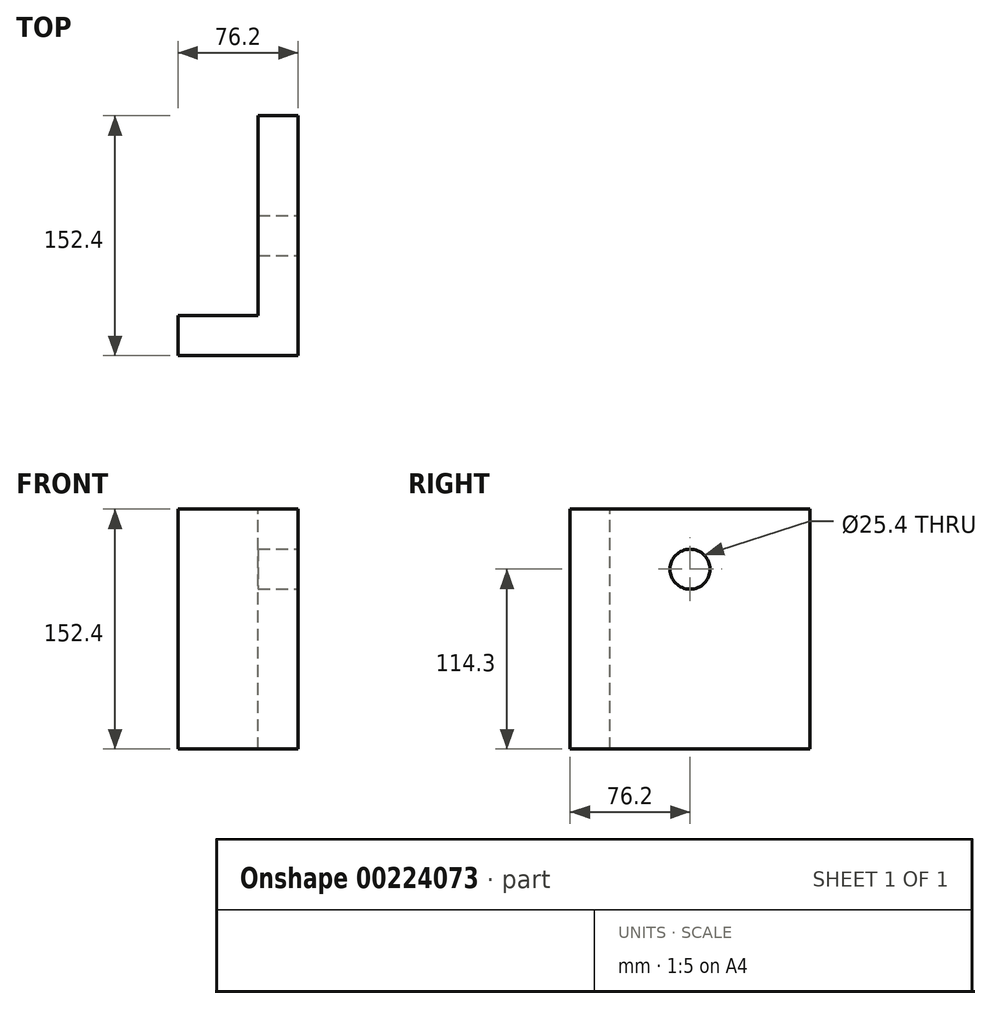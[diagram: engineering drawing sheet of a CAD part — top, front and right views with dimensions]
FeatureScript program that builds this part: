
annotation { "Feature Type Name" : "Feature", "Feature Type Description" : "" }
export const myFeature = defineFeature(function(context is Context, id is Id, definition is map)
    precondition{}
    {
        {
            var Q0;
            Q0=qCreatedBy(makeId("Top.planeOp"),FACE);
            var sketch = newSketch(context, id + "F0", { "sketchPlane" : qUnion([Q0])});
            skLineSegment(sketch, "E0", {"start": v(0, 0) * mm, "end": v(0, 152.4) * mm});
            skLineSegment(sketch, "E1", {"start": v(0, 152.4) * mm, "end": v(-25.4, 152.4) * mm});
            skLineSegment(sketch, "E2", {"start": v(-25.4, 152.4) * mm, "end": v(-25.4, 25.4) * mm});
            skLineSegment(sketch, "E3", {"start": v(-25.4, 25.4) * mm, "end": v(-76.2, 25.4) * mm});
            skLineSegment(sketch, "E4", {"start": v(-76.2, 25.4) * mm, "end": v(-76.2, 0) * mm});
            skLineSegment(sketch, "E5", {"start": v(-76.2, 0) * mm, "end": v(0, 0) * mm});
            skSolve(sketch);
        }
        {
            var Q0;
            Q0=makeQuery(id+"F0.imprint","IMPRINT",FACE,{"disambiguationData":[TD([[makeQuery(id+"F0.imprint","IMPRINT",EDGE,{"derivedFrom":sQuery(id+"F0.wireOp",EDGE,"E0")}),1.0]])]});
            extrude(context, id + "F1", {"entities" : qUnion([Q0]), "endBound" : BoundingType.SYMMETRIC, "oppositeDirection" : true, "depth" : 152.4 * mm});
        }
        {
            var Q0;
            Q0=makeQuery(id+"F1.opExtrude","SWEPT_FACE",FACE,{"disambiguationData":[OSD([sQuery(id+"F0.wireOp",EDGE,"E0")])]});
            var sketch = newSketch(context, id + "F2", { "sketchPlane" : qUnion([Q0])});
            skCircle(sketch, "E6", {"center": v(76.2, 38.1) * mm, "radius": 12.7 * mm});
            skSolve(sketch);
        }
        {
            var Q0;
            Q0=makeQuery(id+"F2.imprint","IMPRINT",FACE,{"disambiguationData":[TD([[makeQuery(id+"F2.imprint","IMPRINT",EDGE,{"derivedFrom":sQuery(id+"F2.wireOp",EDGE,"E6")}),1.0]])]});
            extrude(context, id + "F3", {"entities" : qUnion([Q0]), "operationType" : NewBodyOperationType.REMOVE, "oppositeDirection" : true, "depth" : 33.53 * mm});
        }
    });
